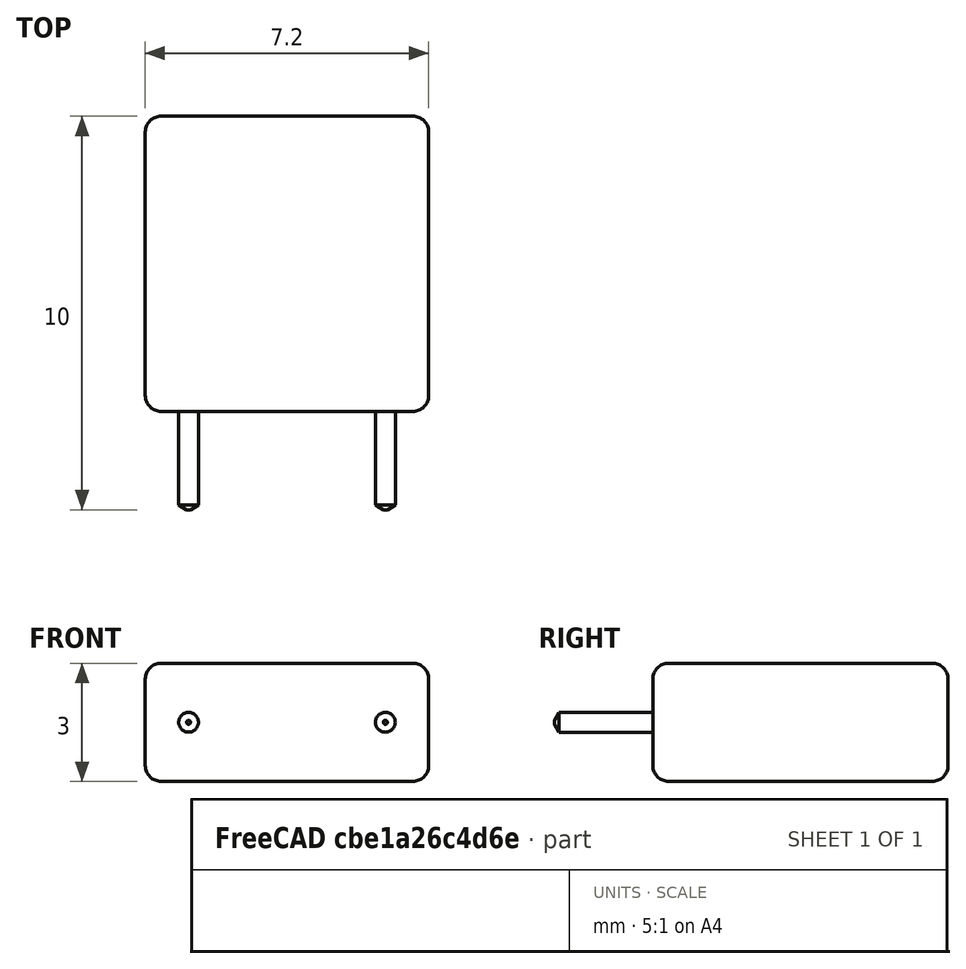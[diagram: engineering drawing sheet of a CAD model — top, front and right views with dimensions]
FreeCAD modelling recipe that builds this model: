
FCSTD DOCUMENT  (FreeCAD 0.17R13528 (Git))
Label: WIMA_C_Case
License: All rights reserved
LicenseURL: http://en.wikipedia.org/wiki/All_rights_reserved
objects: Part::Part2DObjectPython×6, Part::Feature×1
note: 7 computed .brp shape members not serialized (recipe doc carries the construction recipe); baked Part::Feature solids carry a one-line shape summary decoded from their .brp

FEATURE [Part::Part2DObjectPython] ShapeString  label="F_WIMA"  # Draft 2D object (typed FeaturePython)
  FontFile = <userpath>/Desktop/Freecad Projects/calibrib.ttf
  Placement = pos=(-0.75,3.5,1.51) rot=(0,0,1;0rad)
  Size = 1.75
  String = WIMA
  Tracking = 0
FEATURE [Part::Part2DObjectPython] ShapeString001  label="F_Vaule/Rating"  # Draft 2D object (typed FeaturePython)
  FontFile = <userpath>/Desktop/Freecad Projects/calibrib.ttf
  Placement = pos=(-0.65,2.25,1.51) rot=(0,0,1;0rad)
  Size = 1
  String = .001/400V
  Tracking = 0
FEATURE [Part::Part2DObjectPython] ShapeString002  label="F_Tolerance"  # Draft 2D object (typed FeaturePython)
  FontFile = <userpath>/Desktop/Freecad Projects/calibrib.ttf
  Placement = pos=(-0.65,1,1.51) rot=(0,0,1;0rad)
  Size = 1
  String = 10
  Tracking = 0
FEATURE [Part::Part2DObjectPython] ShapeString003  label="B_WIMA"  # Draft 2D object (typed FeaturePython)
  FontFile = <userpath>/Desktop/Freecad Projects/calibrib.ttf
  Placement = pos=(5,3.5,-1.51) rot=(0,1,0;3.14159rad)
  Size = 1.75
  String = WIMA
  Tracking = 0
FEATURE [Part::Part2DObjectPython] ShapeString004  label="B_Value/Tolerance"  # Draft 2D object (typed FeaturePython)
  FontFile = <userpath>/Desktop/Freecad Projects/calibrib.ttf
  Placement = pos=(4.9,2.25,-1.51) rot=(0,1,0;3.14159rad)
  Size = 1
  String = .001/400V
  Tracking = 0
FEATURE [Part::Part2DObjectPython] ShapeString005  label="B_Tolerance"  # Draft 2D object (typed FeaturePython)
  FontFile = <userpath>/Desktop/Freecad Projects/calibrib.ttf
  Placement = pos=(4.9,1,-1.51) rot=(0,1,0;3.14159rad)
  Size = 1
  String = 10
  Tracking = 0
FEATURE [Part::Feature] Part__Feature001  label="WIMA_C_Case"
  shape: bbox 7.2 x 10 x 3 mm, 36 faces (baked)
